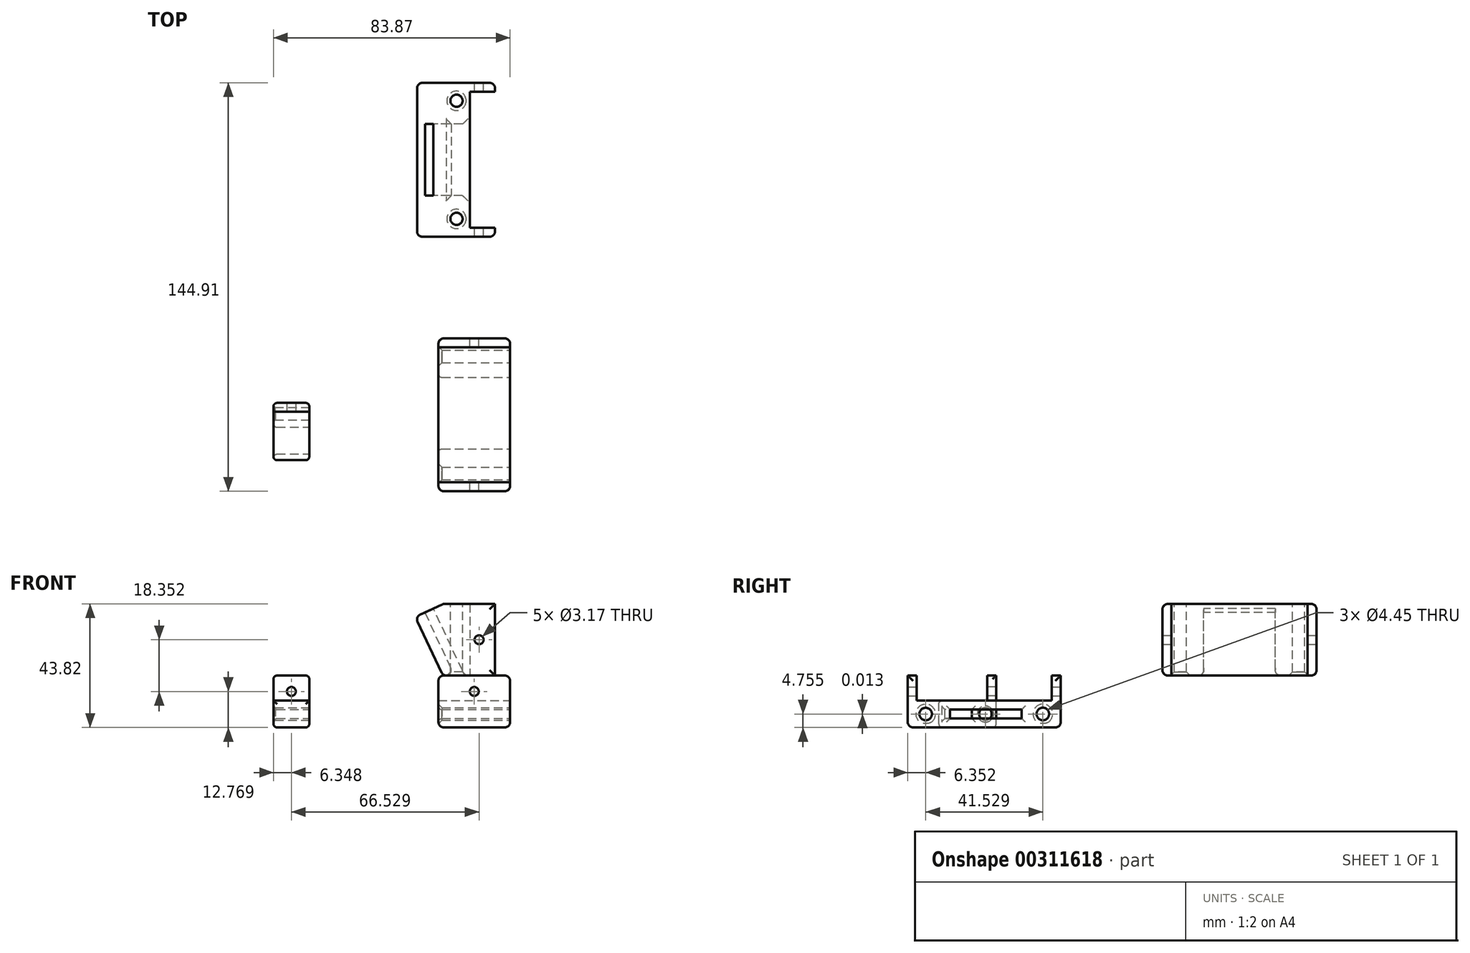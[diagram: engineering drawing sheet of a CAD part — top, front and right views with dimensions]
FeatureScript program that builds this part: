
annotation { "Feature Type Name" : "Feature", "Feature Type Description" : "" }
export const myFeature = defineFeature(function(context is Context, id is Id, definition is map)
    precondition{}
    {
        {
            var Q0;
            Q0=qCreatedBy(makeId("Top.planeOp"),FACE);
            var sketch = newSketch(context, id + "F0", { "sketchPlane" : qUnion([Q0])});
            skLineSegment(sketch, "E0.bottom", {"start": v(-15.61, -27.13) * mm, "end": v(9.79, -27.13) * mm});
            skLineSegment(sketch, "E0.top", {"start": v(-15.61, -30.3) * mm, "end": v(9.79, -30.3) * mm});
            skLineSegment(sketch, "E0.left", {"start": v(-15.61, -27.13) * mm, "end": v(-15.61, -30.3) * mm});
            skLineSegment(sketch, "E0.right", {"start": v(9.79, -27.13) * mm, "end": v(9.79, -30.3) * mm});
            skLineSegment(sketch, "E1.bottom", {"start": v(-15.61, 23.92) * mm, "end": v(9.79, 23.92) * mm});
            skLineSegment(sketch, "E1.top", {"start": v(-15.61, 20.75) * mm, "end": v(9.79, 20.75) * mm});
            skLineSegment(sketch, "E1.left", {"start": v(-15.61, 23.92) * mm, "end": v(-15.61, 20.75) * mm});
            skLineSegment(sketch, "E1.right", {"start": v(9.79, 23.92) * mm, "end": v(9.79, 20.75) * mm});
            skSolve(sketch);
        }
        {
            var Q0;
            Q0 = qSketchRegion(id + "F0", true);
            extrude(context, id + "F1", {"entities" : qUnion([Q0]), "depth" : 8.9 * mm});
        }
        {
            var Q0;
            Q0=makeQuery(id+"F1.opExtrude","CAP_FACE",FACE,{"disambiguationData":[OSD([sQuery(id+"F0.wireOp",EDGE,"E0.bottom"),sQuery(id+"F0.wireOp",EDGE,"E0.top"),sQuery(id+"F0.wireOp",EDGE,"E0.left"),sQuery(id+"F0.wireOp",EDGE,"E0.right")])],"isStart":false});
            var sketch = newSketch(context, id + "F2", { "sketchPlane" : qUnion([Q0])});
            skLineSegment(sketch, "E2.bottom", {"start": v(9.79, -30.3) * mm, "end": v(-15.61, -30.3) * mm});
            skLineSegment(sketch, "E2.top", {"start": v(9.79, 23.92) * mm, "end": v(-15.61, 23.92) * mm});
            skLineSegment(sketch, "E2.left", {"start": v(9.79, -30.3) * mm, "end": v(9.79, 23.92) * mm});
            skLineSegment(sketch, "E2.right", {"start": v(-15.61, -30.3) * mm, "end": v(-15.61, 23.92) * mm});
            skSolve(sketch);
        }
        {
            var Q0;
            Q0 = qSketchRegion(id + "F2", true);
            extrude(context, id + "F3", {"entities" : qUnion([Q0]), "depth" : 9.52 * mm});
        }
        {
            var Q0;
            Q0=makeQuery(id+"F1.opExtrude","SWEPT_BODY",BODY,{"disambiguationData":[OSD([sQuery(id+"F0.wireOp",EDGE,"E0.bottom"),sQuery(id+"F0.wireOp",EDGE,"E0.top"),sQuery(id+"F0.wireOp",EDGE,"E0.left"),sQuery(id+"F0.wireOp",EDGE,"E0.right")])]});
            var Q1;
            Q1=makeQuery(id+"F1.opExtrude","SWEPT_BODY",BODY,{"disambiguationData":[OSD([sQuery(id+"F0.wireOp",EDGE,"E1.bottom"),sQuery(id+"F0.wireOp",EDGE,"E1.top"),sQuery(id+"F0.wireOp",EDGE,"E1.left"),sQuery(id+"F0.wireOp",EDGE,"E1.right")])]});
            var Q2;
            Q2=makeQuery(id+"F3.opExtrude","SWEPT_BODY",BODY,{"disambiguationData":[OSD([sQuery(id+"F2.wireOp",EDGE,"E2.bottom"),sQuery(id+"F2.wireOp",EDGE,"E2.top"),sQuery(id+"F2.wireOp",EDGE,"E2.left"),sQuery(id+"F2.wireOp",EDGE,"E2.right")])]});
            booleanBodies(context, id + "F4", {"operationType" : BooleanOperationType.UNION, "tools" : qUnion([Q0, Q1, Q2])});
        }
        {
            var Q0;
            Q0=makeQuery(id+"F4.opBoolean","MERGE",FACE,{"derivedFrom":[makeQuery(id+"F1.opExtrude","SWEPT_FACE",FACE,{"disambiguationData":[OSD([sQuery(id+"F0.wireOp",EDGE,"E0.right")])]}),makeQuery(id+"F1.opExtrude","SWEPT_FACE",FACE,{"disambiguationData":[OSD([sQuery(id+"F0.wireOp",EDGE,"E1.right")])]}),makeQuery(id+"F3.opExtrude","SWEPT_FACE",FACE,{"disambiguationData":[OSD([sQuery(id+"F2.wireOp",EDGE,"E2.left")])]})]});
            var sketch = newSketch(context, id + "F5", { "sketchPlane" : qUnion([Q0])});
            skCircle(sketch, "E3", {"center": v(-23.96, 13.65) * mm, "radius": 2.22 * mm});
            skCircle(sketch, "E4", {"center": v(17.57, 13.67) * mm, "radius": 2.22 * mm});
            skLineSegment(sketch, "E5.bottom", {"start": v(-16.48, 15.24) * mm, "end": v(8.92, 15.24) * mm});
            skLineSegment(sketch, "E5.top", {"start": v(-16.48, 12.07) * mm, "end": v(8.92, 12.07) * mm});
            skLineSegment(sketch, "E5.left", {"start": v(-16.48, 15.24) * mm, "end": v(-16.48, 12.07) * mm});
            skLineSegment(sketch, "E5.right", {"start": v(8.92, 15.24) * mm, "end": v(8.92, 12.07) * mm});
            skSolve(sketch);
        }
        {
            var Q0;
            Q0 = qSketchRegion(id + "F5", true);
            extrude(context, id + "F6", {"entities" : qUnion([Q0]), "operationType" : NewBodyOperationType.REMOVE, "oppositeDirection" : true, "depth" : 50.8 * mm});
        }
        {
            var Q0;
            Q0=makeQuery(id+"F6.boolean.opBoolean","COPY",EDGE,{"derivedFrom":makeQuery(id+"F6.opExtrude","CAP_EDGE",EDGE,{"disambiguationData":[OSD([sQuery(id+"F5.wireOp",EDGE,"E5.bottom")])],"isStart":true})});
            var Q1;
            Q1=makeQuery(id+"F6.boolean.opBoolean","COPY",EDGE,{"derivedFrom":makeQuery(id+"F6.opExtrude","CAP_EDGE",EDGE,{"disambiguationData":[OSD([sQuery(id+"F5.wireOp",EDGE,"E5.left")])],"isStart":true})});
            var Q2;
            Q2=makeQuery(id+"F6.boolean.opBoolean","COPY",EDGE,{"derivedFrom":makeQuery(id+"F6.opExtrude","CAP_EDGE",EDGE,{"disambiguationData":[OSD([sQuery(id+"F5.wireOp",EDGE,"E5.top")])],"isStart":true})});
            var Q3;
            Q3=makeQuery(id+"F6.boolean.opBoolean","COPY",EDGE,{"derivedFrom":makeQuery(id+"F6.opExtrude","CAP_EDGE",EDGE,{"disambiguationData":[OSD([sQuery(id+"F5.wireOp",EDGE,"E5.right")])],"isStart":true})});
            var Q4;
            Q4=makeQuery(id+"F6.boolean.opBoolean","INTERSECT",EDGE,{"derivedFrom":[makeQuery(id+"F4.opBoolean","MERGE",FACE,{"derivedFrom":[makeQuery(id+"F1.opExtrude","SWEPT_FACE",FACE,{"disambiguationData":[OSD([sQuery(id+"F0.wireOp",EDGE,"E0.left")])]}),makeQuery(id+"F1.opExtrude","SWEPT_FACE",FACE,{"disambiguationData":[OSD([sQuery(id+"F0.wireOp",EDGE,"E1.left")])]}),makeQuery(id+"F3.opExtrude","SWEPT_FACE",FACE,{"disambiguationData":[OSD([sQuery(id+"F2.wireOp",EDGE,"E2.right")])]})]}),makeQuery(id+"F6.opExtrude","SWEPT_FACE",FACE,{"disambiguationData":[OSD([sQuery(id+"F5.wireOp",EDGE,"E5.right")])]})]});
            var Q5;
            Q5=makeQuery(id+"F6.boolean.opBoolean","INTERSECT",EDGE,{"derivedFrom":[makeQuery(id+"F4.opBoolean","MERGE",FACE,{"derivedFrom":[makeQuery(id+"F1.opExtrude","SWEPT_FACE",FACE,{"disambiguationData":[OSD([sQuery(id+"F0.wireOp",EDGE,"E0.left")])]}),makeQuery(id+"F1.opExtrude","SWEPT_FACE",FACE,{"disambiguationData":[OSD([sQuery(id+"F0.wireOp",EDGE,"E1.left")])]}),makeQuery(id+"F3.opExtrude","SWEPT_FACE",FACE,{"disambiguationData":[OSD([sQuery(id+"F2.wireOp",EDGE,"E2.right")])]})]}),makeQuery(id+"F6.opExtrude","SWEPT_FACE",FACE,{"disambiguationData":[OSD([sQuery(id+"F5.wireOp",EDGE,"E5.bottom")])]})]});
            var Q6;
            Q6=makeQuery(id+"F6.boolean.opBoolean","INTERSECT",EDGE,{"derivedFrom":[makeQuery(id+"F4.opBoolean","MERGE",FACE,{"derivedFrom":[makeQuery(id+"F1.opExtrude","SWEPT_FACE",FACE,{"disambiguationData":[OSD([sQuery(id+"F0.wireOp",EDGE,"E0.left")])]}),makeQuery(id+"F1.opExtrude","SWEPT_FACE",FACE,{"disambiguationData":[OSD([sQuery(id+"F0.wireOp",EDGE,"E1.left")])]}),makeQuery(id+"F3.opExtrude","SWEPT_FACE",FACE,{"disambiguationData":[OSD([sQuery(id+"F2.wireOp",EDGE,"E2.right")])]})]}),makeQuery(id+"F6.opExtrude","SWEPT_FACE",FACE,{"disambiguationData":[OSD([sQuery(id+"F5.wireOp",EDGE,"E5.top")])]})]});
            var Q7;
            Q7=makeQuery(id+"F6.boolean.opBoolean","INTERSECT",EDGE,{"derivedFrom":[makeQuery(id+"F4.opBoolean","MERGE",FACE,{"derivedFrom":[makeQuery(id+"F1.opExtrude","SWEPT_FACE",FACE,{"disambiguationData":[OSD([sQuery(id+"F0.wireOp",EDGE,"E0.left")])]}),makeQuery(id+"F1.opExtrude","SWEPT_FACE",FACE,{"disambiguationData":[OSD([sQuery(id+"F0.wireOp",EDGE,"E1.left")])]}),makeQuery(id+"F3.opExtrude","SWEPT_FACE",FACE,{"disambiguationData":[OSD([sQuery(id+"F2.wireOp",EDGE,"E2.right")])]})]}),makeQuery(id+"F6.opExtrude","SWEPT_FACE",FACE,{"disambiguationData":[OSD([sQuery(id+"F5.wireOp",EDGE,"E5.left")])]})]});
            fillet(context, id + "F7", {"entities" : qUnion([Q0, Q1, Q2, Q3, Q4, Q5, Q6, Q7]), "radius" : 1.27 * mm, "tangentPropagation" : true, "allowEdgeOverflow" : false});
        }
        {
            var Q0;
            Q0=makeQuery(id+"F6.boolean.opBoolean","INTERSECT",EDGE,{"derivedFrom":[makeQuery(id+"F4.opBoolean","MERGE",FACE,{"derivedFrom":[makeQuery(id+"F1.opExtrude","SWEPT_FACE",FACE,{"disambiguationData":[OSD([sQuery(id+"F0.wireOp",EDGE,"E0.left")])]}),makeQuery(id+"F1.opExtrude","SWEPT_FACE",FACE,{"disambiguationData":[OSD([sQuery(id+"F0.wireOp",EDGE,"E1.left")])]}),makeQuery(id+"F3.opExtrude","SWEPT_FACE",FACE,{"disambiguationData":[OSD([sQuery(id+"F2.wireOp",EDGE,"E2.right")])]})]}),makeQuery(id+"F6.opExtrude","SWEPT_FACE",FACE,{"disambiguationData":[OSD([sQuery(id+"F5.wireOp",EDGE,"E4")])]})]});
            var Q1;
            Q1=makeQuery(id+"F6.boolean.opBoolean","INTERSECT",EDGE,{"derivedFrom":[makeQuery(id+"F4.opBoolean","MERGE",FACE,{"derivedFrom":[makeQuery(id+"F1.opExtrude","SWEPT_FACE",FACE,{"disambiguationData":[OSD([sQuery(id+"F0.wireOp",EDGE,"E0.left")])]}),makeQuery(id+"F1.opExtrude","SWEPT_FACE",FACE,{"disambiguationData":[OSD([sQuery(id+"F0.wireOp",EDGE,"E1.left")])]}),makeQuery(id+"F3.opExtrude","SWEPT_FACE",FACE,{"disambiguationData":[OSD([sQuery(id+"F2.wireOp",EDGE,"E2.right")])]})]}),makeQuery(id+"F6.opExtrude","SWEPT_FACE",FACE,{"disambiguationData":[OSD([sQuery(id+"F5.wireOp",EDGE,"E3")])]})]});
            var Q2;
            Q2=makeQuery(id+"F6.boolean.opBoolean","COPY",EDGE,{"derivedFrom":makeQuery(id+"F6.opExtrude","CAP_EDGE",EDGE,{"disambiguationData":[OSD([sQuery(id+"F5.wireOp",EDGE,"E3")])],"isStart":true})});
            var Q3;
            Q3=makeQuery(id+"F6.boolean.opBoolean","COPY",EDGE,{"derivedFrom":makeQuery(id+"F6.opExtrude","CAP_EDGE",EDGE,{"disambiguationData":[OSD([sQuery(id+"F5.wireOp",EDGE,"E4")])],"isStart":true})});
            chamfer(context, id + "F8", {"entities" : qUnion([Q0, Q1, Q2, Q3]), "width" : 1.27 * mm, "tangentPropagation" : true});
        }
        {
            var Q0;
            Q0=makeQuery(id+"F3.opExtrude","CAP_EDGE",EDGE,{"disambiguationData":[OSD([sQuery(id+"F2.wireOp",EDGE,"E2.left")])],"isStart":false});
            var Q1;
            Q1=makeQuery(id+"F3.opExtrude","CAP_EDGE",EDGE,{"disambiguationData":[OSD([sQuery(id+"F2.wireOp",EDGE,"E2.bottom")])],"isStart":false});
            var Q2;
            Q2=makeQuery(id+"F3.opExtrude","CAP_EDGE",EDGE,{"disambiguationData":[OSD([sQuery(id+"F2.wireOp",EDGE,"E2.top")])],"isStart":false});
            var Q3;
            Q3=makeQuery(id+"F3.opExtrude","CAP_EDGE",EDGE,{"disambiguationData":[OSD([sQuery(id+"F2.wireOp",EDGE,"E2.right")])],"isStart":false});
            var Q4;
            Q4=makeQuery(id+"F1.opExtrude","CAP_EDGE",EDGE,{"disambiguationData":[OSD([sQuery(id+"F0.wireOp",EDGE,"E0.right")])],"isStart":true});
            var Q5;
            Q5=makeQuery(id+"F1.opExtrude","CAP_EDGE",EDGE,{"disambiguationData":[OSD([sQuery(id+"F0.wireOp",EDGE,"E1.right")])],"isStart":true});
            var Q6;
            Q6=makeQuery(id+"F4.opBoolean","MERGE",EDGE,{"derivedFrom":[makeQuery(id+"F1.opExtrude","SWEPT_EDGE",EDGE,{"disambiguationData":[OSD([sQuery(id+"F0.wireOp",EDGE,"E1.bottom"),sQuery(id+"F0.wireOp",EDGE,"E1.right")])]}),makeQuery(id+"F3.opExtrude","SWEPT_EDGE",EDGE,{"disambiguationData":[OSD([sQuery(id+"F2.wireOp",EDGE,"E2.top"),sQuery(id+"F2.wireOp",EDGE,"E2.left")])]})]});
            var Q7;
            Q7=makeQuery(id+"F4.opBoolean","MERGE",EDGE,{"derivedFrom":[makeQuery(id+"F1.opExtrude","SWEPT_EDGE",EDGE,{"disambiguationData":[OSD([sQuery(id+"F0.wireOp",EDGE,"E0.top"),sQuery(id+"F0.wireOp",EDGE,"E0.right")])]}),makeQuery(id+"F3.opExtrude","SWEPT_EDGE",EDGE,{"disambiguationData":[OSD([sQuery(id+"F2.wireOp",EDGE,"E2.bottom"),sQuery(id+"F2.wireOp",EDGE,"E2.left")])]})]});
            var Q8;
            Q8=makeQuery(id+"F4.opBoolean","MERGE",EDGE,{"derivedFrom":[makeQuery(id+"F1.opExtrude","SWEPT_EDGE",EDGE,{"disambiguationData":[OSD([sQuery(id+"F0.wireOp",EDGE,"E0.top"),sQuery(id+"F0.wireOp",EDGE,"E0.left")])]}),makeQuery(id+"F3.opExtrude","SWEPT_EDGE",EDGE,{"disambiguationData":[OSD([sQuery(id+"F2.wireOp",EDGE,"E2.bottom"),sQuery(id+"F2.wireOp",EDGE,"E2.right")])]})]});
            var Q9;
            Q9=makeQuery(id+"F1.opExtrude","CAP_EDGE",EDGE,{"disambiguationData":[OSD([sQuery(id+"F0.wireOp",EDGE,"E0.left")])],"isStart":true});
            var Q10;
            Q10=makeQuery(id+"F4.opBoolean","MERGE",EDGE,{"derivedFrom":[makeQuery(id+"F1.opExtrude","SWEPT_EDGE",EDGE,{"disambiguationData":[OSD([sQuery(id+"F0.wireOp",EDGE,"E1.bottom"),sQuery(id+"F0.wireOp",EDGE,"E1.left")])]}),makeQuery(id+"F3.opExtrude","SWEPT_EDGE",EDGE,{"disambiguationData":[OSD([sQuery(id+"F2.wireOp",EDGE,"E2.top"),sQuery(id+"F2.wireOp",EDGE,"E2.right")])]})]});
            var Q11;
            Q11=makeQuery(id+"F1.opExtrude","CAP_EDGE",EDGE,{"disambiguationData":[OSD([sQuery(id+"F0.wireOp",EDGE,"E1.left")])],"isStart":true});
            fillet(context, id + "F9", {"entities" : qUnion([Q0, Q1, Q2, Q3, Q4, Q5, Q6, Q7, Q8, Q9, Q10, Q11]), "radius" : 1.9 * mm, "tangentPropagation" : true, "allowEdgeOverflow" : false});
        }
        {
            var Q0;
            Q0=makeQuery(id+"F1.opExtrude","SWEPT_FACE",FACE,{"disambiguationData":[OSD([sQuery(id+"F0.wireOp",EDGE,"E1.top")])]});
            var sketch = newSketch(context, id + "F10", { "sketchPlane" : qUnion([Q0])});
            skCircle(sketch, "E6", {"center": v(-2.91, 5.65) * mm, "radius": 1.59 * mm});
            skSolve(sketch);
        }
        {
            var Q0;
            Q0 = qSketchRegion(id + "F10", true);
            extrude(context, id + "F11", {"entities" : qUnion([Q0]), "operationType" : NewBodyOperationType.REMOVE, "endBound" : BoundingType.SYMMETRIC, "oppositeDirection" : true, "depth" : 127 * mm});
        }
        {
            var Q0;
            Q0=qCreatedBy(makeId("Top.planeOp"),FACE);
            var sketch = newSketch(context, id + "F12", { "sketchPlane" : qUnion([Q0])});
            skLineSegment(sketch, "E7.bottom", {"start": v(-61.38, -53.2) * mm, "end": v(-74.08, -53.2) * mm});
            skLineSegment(sketch, "E7.top", {"start": v(-61.38, -50.03) * mm, "end": v(-74.08, -50.03) * mm});
            skLineSegment(sketch, "E7.left", {"start": v(-61.38, -53.2) * mm, "end": v(-61.38, -50.03) * mm});
            skLineSegment(sketch, "E7.right", {"start": v(-74.08, -53.2) * mm, "end": v(-74.08, -50.03) * mm});
            skSolve(sketch);
        }
        {
            var Q0;
            Q0=makeQuery(id+"F12.imprint","IMPRINT",FACE,{"disambiguationData":[TD([[makeQuery(id+"F12.imprint","IMPRINT",EDGE,{"derivedFrom":sQuery(id+"F12.wireOp",EDGE,"E7.bottom")}),-1.0]])]});
            extrude(context, id + "F13", {"entities" : qUnion([Q0]), "depth" : 8.9 * mm});
        }
        {
            var Q0;
            Q0=makeQuery(id+"F13.opExtrude","CAP_FACE",FACE,{"disambiguationData":[OSD([sQuery(id+"F12.wireOp",EDGE,"E7.bottom"),sQuery(id+"F12.wireOp",EDGE,"E7.top"),sQuery(id+"F12.wireOp",EDGE,"E7.left"),sQuery(id+"F12.wireOp",EDGE,"E7.right")])],"isStart":false});
            var sketch = newSketch(context, id + "F14", { "sketchPlane" : qUnion([Q0])});
            skLineSegment(sketch, "E8.bottom", {"start": v(-61.38, -50.03) * mm, "end": v(-74.08, -50.03) * mm});
            skLineSegment(sketch, "E8.top", {"start": v(-61.38, -32.88) * mm, "end": v(-74.08, -32.88) * mm});
            skLineSegment(sketch, "E8.left", {"start": v(-61.38, -50.03) * mm, "end": v(-61.38, -32.88) * mm});
            skLineSegment(sketch, "E8.right", {"start": v(-74.08, -50.03) * mm, "end": v(-74.08, -32.88) * mm});
            skLineSegment(sketch, "E9.bottom", {"start": v(-74.08, -50.03) * mm, "end": v(-61.38, -50.03) * mm});
            skLineSegment(sketch, "E9.top", {"start": v(-74.08, -53.2) * mm, "end": v(-61.38, -53.2) * mm});
            skLineSegment(sketch, "E9.left", {"start": v(-74.08, -50.03) * mm, "end": v(-74.08, -53.2) * mm});
            skLineSegment(sketch, "E9.right", {"start": v(-61.38, -50.03) * mm, "end": v(-61.38, -53.2) * mm});
            skSolve(sketch);
        }
        {
            var Q0;
            Q0 = qSketchRegion(id + "F14", true);
            extrude(context, id + "F15", {"entities" : qUnion([Q0]), "operationType" : NewBodyOperationType.ADD, "depth" : 9.52 * mm});
        }
        {
            var Q0;
            Q0=makeQuery(id+"F15.boolean.opBoolean","MERGE",FACE,{"derivedFrom":[makeQuery(id+"F13.opExtrude","SWEPT_FACE",FACE,{"disambiguationData":[OSD([sQuery(id+"F12.wireOp",EDGE,"E7.left")])]}),makeQuery(id+"F15.opExtrude","SWEPT_FACE",FACE,{"disambiguationData":[OSD([sQuery(id+"F14.wireOp",EDGE,"E8.left"),sQuery(id+"F14.wireOp",EDGE,"E9.right")])]})]});
            var sketch = newSketch(context, id + "F16", { "sketchPlane" : qUnion([Q0])});
            skCircle(sketch, "E10", {"center": v(-49.4, 13.65) * mm, "radius": 2.22 * mm});
            skLineSegment(sketch, "E11.bottom", {"start": v(-44.57, 15.23) * mm, "end": v(-35.04, 15.23) * mm});
            skLineSegment(sketch, "E11.top", {"start": v(-44.57, 12.06) * mm, "end": v(-35.04, 12.06) * mm});
            skLineSegment(sketch, "E11.left", {"start": v(-44.57, 15.23) * mm, "end": v(-44.57, 12.06) * mm});
            skLineSegment(sketch, "E11.right", {"start": v(-35.04, 15.23) * mm, "end": v(-35.04, 12.06) * mm});
            skSolve(sketch);
        }
        {
            var Q0;
            Q0 = qSketchRegion(id + "F16", true);
            extrude(context, id + "F17", {"entities" : qUnion([Q0]), "operationType" : NewBodyOperationType.REMOVE, "oppositeDirection" : true, "depth" : 25.4 * mm});
        }
        {
            var Q0;
            Q0=makeQuery(id+"F17.boolean.opBoolean","COPY",EDGE,{"derivedFrom":makeQuery(id+"F17.opExtrude","CAP_EDGE",EDGE,{"disambiguationData":[OSD([sQuery(id+"F16.wireOp",EDGE,"E11.bottom")])],"isStart":true})});
            var Q1;
            Q1=makeQuery(id+"F17.boolean.opBoolean","COPY",EDGE,{"derivedFrom":makeQuery(id+"F17.opExtrude","CAP_EDGE",EDGE,{"disambiguationData":[OSD([sQuery(id+"F16.wireOp",EDGE,"E11.left")])],"isStart":true})});
            var Q2;
            Q2=makeQuery(id+"F17.boolean.opBoolean","COPY",EDGE,{"derivedFrom":makeQuery(id+"F17.opExtrude","CAP_EDGE",EDGE,{"disambiguationData":[OSD([sQuery(id+"F16.wireOp",EDGE,"E11.top")])],"isStart":true})});
            var Q3;
            Q3=makeQuery(id+"F17.boolean.opBoolean","COPY",EDGE,{"derivedFrom":makeQuery(id+"F17.opExtrude","CAP_EDGE",EDGE,{"disambiguationData":[OSD([sQuery(id+"F16.wireOp",EDGE,"E11.right")])],"isStart":true})});
            var Q4;
            Q4=makeQuery(id+"F17.boolean.opBoolean","INTERSECT",EDGE,{"derivedFrom":[makeQuery(id+"F15.boolean.opBoolean","MERGE",FACE,{"derivedFrom":[makeQuery(id+"F13.opExtrude","SWEPT_FACE",FACE,{"disambiguationData":[OSD([sQuery(id+"F12.wireOp",EDGE,"E7.right")])]}),makeQuery(id+"F15.opExtrude","SWEPT_FACE",FACE,{"disambiguationData":[OSD([sQuery(id+"F14.wireOp",EDGE,"E8.right"),sQuery(id+"F14.wireOp",EDGE,"E9.left")])]})]}),makeQuery(id+"F17.opExtrude","SWEPT_FACE",FACE,{"disambiguationData":[OSD([sQuery(id+"F16.wireOp",EDGE,"E11.bottom")])]})]});
            var Q5;
            Q5=makeQuery(id+"F17.boolean.opBoolean","INTERSECT",EDGE,{"derivedFrom":[makeQuery(id+"F15.boolean.opBoolean","MERGE",FACE,{"derivedFrom":[makeQuery(id+"F13.opExtrude","SWEPT_FACE",FACE,{"disambiguationData":[OSD([sQuery(id+"F12.wireOp",EDGE,"E7.right")])]}),makeQuery(id+"F15.opExtrude","SWEPT_FACE",FACE,{"disambiguationData":[OSD([sQuery(id+"F14.wireOp",EDGE,"E8.right"),sQuery(id+"F14.wireOp",EDGE,"E9.left")])]})]}),makeQuery(id+"F17.opExtrude","SWEPT_FACE",FACE,{"disambiguationData":[OSD([sQuery(id+"F16.wireOp",EDGE,"E11.right")])]})]});
            var Q6;
            Q6=makeQuery(id+"F17.boolean.opBoolean","INTERSECT",EDGE,{"derivedFrom":[makeQuery(id+"F15.boolean.opBoolean","MERGE",FACE,{"derivedFrom":[makeQuery(id+"F13.opExtrude","SWEPT_FACE",FACE,{"disambiguationData":[OSD([sQuery(id+"F12.wireOp",EDGE,"E7.right")])]}),makeQuery(id+"F15.opExtrude","SWEPT_FACE",FACE,{"disambiguationData":[OSD([sQuery(id+"F14.wireOp",EDGE,"E8.right"),sQuery(id+"F14.wireOp",EDGE,"E9.left")])]})]}),makeQuery(id+"F17.opExtrude","SWEPT_FACE",FACE,{"disambiguationData":[OSD([sQuery(id+"F16.wireOp",EDGE,"E11.top")])]})]});
            var Q7;
            Q7=makeQuery(id+"F17.boolean.opBoolean","INTERSECT",EDGE,{"derivedFrom":[makeQuery(id+"F15.boolean.opBoolean","MERGE",FACE,{"derivedFrom":[makeQuery(id+"F13.opExtrude","SWEPT_FACE",FACE,{"disambiguationData":[OSD([sQuery(id+"F12.wireOp",EDGE,"E7.right")])]}),makeQuery(id+"F15.opExtrude","SWEPT_FACE",FACE,{"disambiguationData":[OSD([sQuery(id+"F14.wireOp",EDGE,"E8.right"),sQuery(id+"F14.wireOp",EDGE,"E9.left")])]})]}),makeQuery(id+"F17.opExtrude","SWEPT_FACE",FACE,{"disambiguationData":[OSD([sQuery(id+"F16.wireOp",EDGE,"E11.left")])]})]});
            fillet(context, id + "F18", {"entities" : qUnion([Q0, Q1, Q2, Q3, Q4, Q5, Q6, Q7]), "radius" : 1.27 * mm, "tangentPropagation" : true, "allowEdgeOverflow" : false});
        }
        {
            var Q0;
            Q0=makeQuery(id+"F17.boolean.opBoolean","INTERSECT",EDGE,{"derivedFrom":[makeQuery(id+"F15.boolean.opBoolean","MERGE",FACE,{"derivedFrom":[makeQuery(id+"F13.opExtrude","SWEPT_FACE",FACE,{"disambiguationData":[OSD([sQuery(id+"F12.wireOp",EDGE,"E7.right")])]}),makeQuery(id+"F15.opExtrude","SWEPT_FACE",FACE,{"disambiguationData":[OSD([sQuery(id+"F14.wireOp",EDGE,"E8.right"),sQuery(id+"F14.wireOp",EDGE,"E9.left")])]})]}),makeQuery(id+"F17.opExtrude","SWEPT_FACE",FACE,{"disambiguationData":[OSD([sQuery(id+"F16.wireOp",EDGE,"E10")])]})]});
            var Q1;
            Q1=makeQuery(id+"F17.boolean.opBoolean","COPY",EDGE,{"derivedFrom":makeQuery(id+"F17.opExtrude","CAP_EDGE",EDGE,{"disambiguationData":[OSD([sQuery(id+"F16.wireOp",EDGE,"E10")])],"isStart":true})});
            chamfer(context, id + "F19", {"entities" : qUnion([Q0, Q1]), "width" : 0.64 * mm, "tangentPropagation" : true});
        }
        {
            var Q0;
            Q0=makeQuery(id+"F15.opExtrude","CAP_FACE",FACE,{"disambiguationData":[OSD([sQuery(id+"F14.wireOp",EDGE,"E8.top"),sQuery(id+"F14.wireOp",EDGE,"E8.left"),sQuery(id+"F14.wireOp",EDGE,"E8.right"),sQuery(id+"F14.wireOp",EDGE,"E9.top"),sQuery(id+"F14.wireOp",EDGE,"E9.left"),sQuery(id+"F14.wireOp",EDGE,"E9.right")])],"isStart":false});
            var Q1;
            Q1=makeQuery(id+"F15.boolean.opBoolean","MERGE",EDGE,{"derivedFrom":[makeQuery(id+"F13.opExtrude","SWEPT_EDGE",EDGE,{"disambiguationData":[OSD([sQuery(id+"F12.wireOp",EDGE,"E7.bottom"),sQuery(id+"F12.wireOp",EDGE,"E7.left")])]}),makeQuery(id+"F15.opExtrude","SWEPT_EDGE",EDGE,{"disambiguationData":[OSD([sQuery(id+"F14.wireOp",EDGE,"E9.top"),sQuery(id+"F14.wireOp",EDGE,"E9.right")])]})]});
            var Q2;
            Q2=makeQuery(id+"F15.boolean.opBoolean","MERGE",EDGE,{"derivedFrom":[makeQuery(id+"F13.opExtrude","SWEPT_EDGE",EDGE,{"disambiguationData":[OSD([sQuery(id+"F12.wireOp",EDGE,"E7.bottom"),sQuery(id+"F12.wireOp",EDGE,"E7.right")])]}),makeQuery(id+"F15.opExtrude","SWEPT_EDGE",EDGE,{"disambiguationData":[OSD([sQuery(id+"F14.wireOp",EDGE,"E9.top"),sQuery(id+"F14.wireOp",EDGE,"E9.left")])]})]});
            var Q3;
            Q3=makeQuery(id+"F13.opExtrude","CAP_EDGE",EDGE,{"disambiguationData":[OSD([sQuery(id+"F12.wireOp",EDGE,"E7.left")])],"isStart":true});
            var Q4;
            Q4=makeQuery(id+"F15.opExtrude","SWEPT_EDGE",EDGE,{"disambiguationData":[OSD([sQuery(id+"F14.wireOp",EDGE,"E8.top"),sQuery(id+"F14.wireOp",EDGE,"E8.left")])]});
            var Q5;
            Q5=makeQuery(id+"F15.opExtrude","CAP_EDGE",EDGE,{"disambiguationData":[OSD([sQuery(id+"F14.wireOp",EDGE,"E8.top")])],"isStart":true});
            var Q6;
            Q6=makeQuery(id+"F15.opExtrude","SWEPT_EDGE",EDGE,{"disambiguationData":[OSD([sQuery(id+"F14.wireOp",EDGE,"E8.top"),sQuery(id+"F14.wireOp",EDGE,"E8.right")])]});
            var Q7;
            Q7=makeQuery(id+"F13.opExtrude","CAP_EDGE",EDGE,{"disambiguationData":[OSD([sQuery(id+"F12.wireOp",EDGE,"E7.right")])],"isStart":true});
            fillet(context, id + "F20", {"entities" : qUnion([Q0, Q1, Q2, Q3, Q4, Q5, Q6, Q7]), "radius" : 1.27 * mm, "tangentPropagation" : true, "allowEdgeOverflow" : false});
        }
        {
            var Q0;
            Q0=makeQuery(id+"F13.opExtrude","SWEPT_FACE",FACE,{"disambiguationData":[OSD([sQuery(id+"F12.wireOp",EDGE,"E7.top")])]});
            var sketch = newSketch(context, id + "F21", { "sketchPlane" : qUnion([Q0])});
            skCircle(sketch, "E12", {"center": v(67.73, 5.65) * mm, "radius": 1.59 * mm});
            skSolve(sketch);
        }
        {
            var Q0;
            Q0=makeQuery(id+"F21.imprint","IMPRINT",FACE,{"disambiguationData":[TD([[makeQuery(id+"F21.imprint","IMPRINT",EDGE,{"derivedFrom":sQuery(id+"F21.wireOp",EDGE,"E12")}),1.0]])]});
            extrude(context, id + "F22", {"entities" : qUnion([Q0]), "operationType" : NewBodyOperationType.REMOVE, "oppositeDirection" : true, "depth" : 25.4 * mm});
        }
        {
            var Q0;
            Q0=makeQuery(id+"F1.opExtrude","SWEPT_BODY",BODY,{"disambiguationData":[OSD([sQuery(id+"F0.wireOp",EDGE,"E0.bottom"),sQuery(id+"F0.wireOp",EDGE,"E0.top"),sQuery(id+"F0.wireOp",EDGE,"E0.left"),sQuery(id+"F0.wireOp",EDGE,"E0.right")])]});
            var Q1;
            Q1=makeQuery(id+"F1.opExtrude","CAP_EDGE",EDGE,{"disambiguationData":[OSD([sQuery(id+"F0.wireOp",EDGE,"E0.top")])],"isStart":true});
            var Q2;
            Q2=makeQuery(id+"F1.opExtrude","CAP_EDGE",EDGE,{"disambiguationData":[OSD([sQuery(id+"F0.wireOp",EDGE,"E0.top")])],"isStart":true});
            transform(context, id + "F23", {"entities" : qUnion([Q0]), "transformType" : TransformType.ROTATION, "transformAxis" : qUnion([Q2]), "angle" : 180 * degree, "makeCopy" : false});
        }
        {
            var Q0;
            Q0=makeQuery(id+"F13.opExtrude","SWEPT_BODY",BODY,{"disambiguationData":[OSD([sQuery(id+"F12.wireOp",EDGE,"E7.bottom"),sQuery(id+"F12.wireOp",EDGE,"E7.top"),sQuery(id+"F12.wireOp",EDGE,"E7.left"),sQuery(id+"F12.wireOp",EDGE,"E7.right")])]});
            var Q1;
            Q1=makeQuery(id+"F13.opExtrude","CAP_EDGE",EDGE,{"disambiguationData":[OSD([sQuery(id+"F12.wireOp",EDGE,"E7.bottom")])],"isStart":true});
            transform(context, id + "F24", {"entities" : qUnion([Q0]), "transformType" : TransformType.ROTATION, "transformAxis" : qUnion([Q1]), "angle" : 180 * degree, "makeCopy" : false});
        }
        {
            var Q0;
            Q0=qCreatedBy(makeId("Top.planeOp"),FACE);
            var sketch = newSketch(context, id + "F25", { "sketchPlane" : qUnion([Q0])});
            skLineSegment(sketch, "E13.bottom", {"start": v(-13.97, 60.37) * mm, "end": v(-4.44, 60.37) * mm});
            skLineSegment(sketch, "E13.top", {"start": v(-13.97, 5.76) * mm, "end": v(-4.44, 5.76) * mm});
            skLineSegment(sketch, "E13.left", {"start": v(-13.97, 60.37) * mm, "end": v(-13.97, 5.76) * mm});
            skLineSegment(sketch, "E13.right", {"start": v(-4.44, 60.37) * mm, "end": v(-4.44, 5.76) * mm});
            skLineSegment(sketch, "E14.bottom", {"start": v(-4.44, 5.76) * mm, "end": v(4.45, 5.76) * mm});
            skLineSegment(sketch, "E14.top", {"start": v(-4.44, 8.93) * mm, "end": v(4.45, 8.93) * mm});
            skLineSegment(sketch, "E14.left", {"start": v(-4.44, 5.76) * mm, "end": v(-4.44, 8.93) * mm});
            skLineSegment(sketch, "E14.right", {"start": v(4.45, 5.76) * mm, "end": v(4.45, 8.93) * mm});
            skLineSegment(sketch, "E15.bottom", {"start": v(-4.44, 60.37) * mm, "end": v(4.45, 60.37) * mm});
            skLineSegment(sketch, "E15.top", {"start": v(-4.44, 57.2) * mm, "end": v(4.45, 57.2) * mm});
            skLineSegment(sketch, "E15.left", {"start": v(-4.44, 60.37) * mm, "end": v(-4.44, 57.2) * mm});
            skLineSegment(sketch, "E15.right", {"start": v(4.45, 60.37) * mm, "end": v(4.45, 57.2) * mm});
            skSolve(sketch);
        }
        {
            var Q0;
            Q0 = qSketchRegion(id + "F25", true);
            extrude(context, id + "F26", {"entities" : qUnion([Q0]), "depth" : 25.4 * mm});
        }
        {
            var Q0;
            Q0=makeQuery(id+"F26.opExtrude","SWEPT_FACE",FACE,{"disambiguationData":[OSD([sQuery(id+"F25.wireOp",EDGE,"E13.top"),sQuery(id+"F25.wireOp",EDGE,"E14.bottom")])]});
            var sketch = newSketch(context, id + "F27", { "sketchPlane" : qUnion([Q0])});
            skLineSegment(sketch, "E16", {"start": v(-13.97, 0) * mm, "end": v(-23.83, 20.8) * mm});
            skLineSegment(sketch, "E17", {"start": v(-13.97, 25.4) * mm, "end": v(-23.83, 20.8) * mm});
            skSolve(sketch);
        }
        {
            var Q0;
            Q0=makeQuery(id+"F26.opExtrude","SWEPT_FACE",FACE,{"disambiguationData":[OSD([sQuery(id+"F25.wireOp",EDGE,"E13.bottom"),sQuery(id+"F25.wireOp",EDGE,"E15.bottom")])]});
            var sketch = newSketch(context, id + "F28", { "sketchPlane" : qUnion([Q0])});
            skLineSegment(sketch, "E18", {"start": v(13.97, 0) * mm, "end": v(23.7, 20.86) * mm});
            skLineSegment(sketch, "E19", {"start": v(13.97, 25.4) * mm, "end": v(23.7, 20.86) * mm});
            skSolve(sketch);
        }
        {
            var Q0;
            Q0=makeQuery(id+"F27.imprint","IMPRINT",FACE,{"disambiguationData":[TD([[makeQuery(id+"F27.imprint","IMPRINT",EDGE,{"derivedFrom":sQuery(id+"F27.wireOp",EDGE,"E16")}),-1.0]])]});
            extrude(context, id + "F29", {"entities" : qUnion([Q0]), "oppositeDirection" : true, "depth" : 54.6 * mm});
        }
        {
            var Q0;
            Q0=makeQuery(id+"F26.opExtrude","SWEPT_BODY",BODY,{"disambiguationData":[OSD([sQuery(id+"F25.wireOp",EDGE,"E13.bottom"),sQuery(id+"F25.wireOp",EDGE,"E13.top"),sQuery(id+"F25.wireOp",EDGE,"E13.left"),sQuery(id+"F25.wireOp",EDGE,"E13.right"),sQuery(id+"F25.wireOp",EDGE,"E14.bottom"),sQuery(id+"F25.wireOp",EDGE,"E14.top"),sQuery(id+"F25.wireOp",EDGE,"E14.right"),sQuery(id+"F25.wireOp",EDGE,"E15.bottom"),sQuery(id+"F25.wireOp",EDGE,"E15.top"),sQuery(id+"F25.wireOp",EDGE,"E15.right")])]});
            var Q1;
            Q1=makeQuery(id+"F29.opExtrude","SWEPT_BODY",BODY,{"disambiguationData":[OSD([sQuery(id+"F25.wireOp",EDGE,"E13.top"),sQuery(id+"F25.wireOp",EDGE,"E13.left"),sQuery(id+"F27.wireOp",EDGE,"E16"),sQuery(id+"F27.wireOp",EDGE,"E17")])]});
            booleanBodies(context, id + "F30", {"operationType" : BooleanOperationType.UNION, "tools" : qUnion([Q0, Q1])});
        }
        {
            var Q0;
            Q0=makeQuery(id+"F29.opExtrude","SWEPT_FACE",FACE,{"disambiguationData":[OSD([sQuery(id+"F27.wireOp",EDGE,"E17")])]});
            var sketch = newSketch(context, id + "F31", { "sketchPlane" : qUnion([Q0])});
            skLineSegment(sketch, "E20.bottom", {"start": v(-5.72, 45.76) * mm, "end": v(-9.02, 45.76) * mm});
            skLineSegment(sketch, "E20.top", {"start": v(-5.72, 20.36) * mm, "end": v(-9.02, 20.36) * mm});
            skLineSegment(sketch, "E20.left", {"start": v(-5.72, 45.76) * mm, "end": v(-5.72, 20.36) * mm});
            skLineSegment(sketch, "E20.right", {"start": v(-9.02, 45.76) * mm, "end": v(-9.02, 20.36) * mm});
            skSolve(sketch);
        }
        {
            var Q0;
            Q0=makeQuery(id+"F31.imprint","IMPRINT",FACE,{"disambiguationData":[TD([[makeQuery(id+"F31.imprint","IMPRINT",EDGE,{"derivedFrom":sQuery(id+"F31.wireOp",EDGE,"E20.bottom")}),1.0]])]});
            extrude(context, id + "F32", {"entities" : qUnion([Q0]), "operationType" : NewBodyOperationType.REMOVE, "oppositeDirection" : true, "depth" : 50.8 * mm});
        }
        {
            var Q0;
            Q0=makeQuery(id+"F32.boolean.opBoolean","COPY",EDGE,{"derivedFrom":makeQuery(id+"F32.opExtrude","CAP_EDGE",EDGE,{"disambiguationData":[OSD([sQuery(id+"F31.wireOp",EDGE,"E20.left")])],"isStart":true})});
            var Q1;
            Q1=makeQuery(id+"F32.boolean.opBoolean","COPY",EDGE,{"derivedFrom":makeQuery(id+"F32.opExtrude","CAP_EDGE",EDGE,{"disambiguationData":[OSD([sQuery(id+"F31.wireOp",EDGE,"E20.right")])],"isStart":true})});
            var Q2;
            Q2=makeQuery(id+"F32.boolean.opBoolean","COPY",EDGE,{"derivedFrom":makeQuery(id+"F32.opExtrude","CAP_EDGE",EDGE,{"disambiguationData":[OSD([sQuery(id+"F31.wireOp",EDGE,"E20.top")])],"isStart":true})});
            var Q3;
            Q3=makeQuery(id+"F32.boolean.opBoolean","COPY",EDGE,{"derivedFrom":makeQuery(id+"F32.opExtrude","CAP_EDGE",EDGE,{"disambiguationData":[OSD([sQuery(id+"F31.wireOp",EDGE,"E20.bottom")])],"isStart":true})});
            var Q4;
            Q4=makeQuery(id+"F32.boolean.opBoolean","INTERSECT",EDGE,{"derivedFrom":[makeQuery(id+"F26.opExtrude","CAP_FACE",FACE,{"disambiguationData":[OSD([sQuery(id+"F25.wireOp",EDGE,"E13.bottom"),sQuery(id+"F25.wireOp",EDGE,"E13.top"),sQuery(id+"F25.wireOp",EDGE,"E13.left"),sQuery(id+"F25.wireOp",EDGE,"E13.right"),sQuery(id+"F25.wireOp",EDGE,"E14.bottom"),sQuery(id+"F25.wireOp",EDGE,"E14.top"),sQuery(id+"F25.wireOp",EDGE,"E14.right"),sQuery(id+"F25.wireOp",EDGE,"E15.bottom"),sQuery(id+"F25.wireOp",EDGE,"E15.top"),sQuery(id+"F25.wireOp",EDGE,"E15.right")])],"isStart":true}),makeQuery(id+"F32.opExtrude","SWEPT_FACE",FACE,{"disambiguationData":[OSD([sQuery(id+"F31.wireOp",EDGE,"E20.right")])]})]});
            var Q5;
            Q5=makeQuery(id+"F32.boolean.opBoolean","INTERSECT",EDGE,{"derivedFrom":[makeQuery(id+"F26.opExtrude","CAP_FACE",FACE,{"disambiguationData":[OSD([sQuery(id+"F25.wireOp",EDGE,"E13.bottom"),sQuery(id+"F25.wireOp",EDGE,"E13.top"),sQuery(id+"F25.wireOp",EDGE,"E13.left"),sQuery(id+"F25.wireOp",EDGE,"E13.right"),sQuery(id+"F25.wireOp",EDGE,"E14.bottom"),sQuery(id+"F25.wireOp",EDGE,"E14.top"),sQuery(id+"F25.wireOp",EDGE,"E14.right"),sQuery(id+"F25.wireOp",EDGE,"E15.bottom"),sQuery(id+"F25.wireOp",EDGE,"E15.top"),sQuery(id+"F25.wireOp",EDGE,"E15.right")])],"isStart":true}),makeQuery(id+"F32.opExtrude","SWEPT_FACE",FACE,{"disambiguationData":[OSD([sQuery(id+"F31.wireOp",EDGE,"E20.top")])]})]});
            var Q6;
            Q6=makeQuery(id+"F32.boolean.opBoolean","INTERSECT",EDGE,{"derivedFrom":[makeQuery(id+"F26.opExtrude","CAP_FACE",FACE,{"disambiguationData":[OSD([sQuery(id+"F25.wireOp",EDGE,"E13.bottom"),sQuery(id+"F25.wireOp",EDGE,"E13.top"),sQuery(id+"F25.wireOp",EDGE,"E13.left"),sQuery(id+"F25.wireOp",EDGE,"E13.right"),sQuery(id+"F25.wireOp",EDGE,"E14.bottom"),sQuery(id+"F25.wireOp",EDGE,"E14.top"),sQuery(id+"F25.wireOp",EDGE,"E14.right"),sQuery(id+"F25.wireOp",EDGE,"E15.bottom"),sQuery(id+"F25.wireOp",EDGE,"E15.top"),sQuery(id+"F25.wireOp",EDGE,"E15.right")])],"isStart":true}),makeQuery(id+"F32.opExtrude","SWEPT_FACE",FACE,{"disambiguationData":[OSD([sQuery(id+"F31.wireOp",EDGE,"E20.bottom")])]})]});
            var Q7;
            Q7=makeQuery(id+"F32.boolean.opBoolean","INTERSECT",EDGE,{"derivedFrom":[makeQuery(id+"F26.opExtrude","CAP_FACE",FACE,{"disambiguationData":[OSD([sQuery(id+"F25.wireOp",EDGE,"E13.bottom"),sQuery(id+"F25.wireOp",EDGE,"E13.top"),sQuery(id+"F25.wireOp",EDGE,"E13.left"),sQuery(id+"F25.wireOp",EDGE,"E13.right"),sQuery(id+"F25.wireOp",EDGE,"E14.bottom"),sQuery(id+"F25.wireOp",EDGE,"E14.top"),sQuery(id+"F25.wireOp",EDGE,"E14.right"),sQuery(id+"F25.wireOp",EDGE,"E15.bottom"),sQuery(id+"F25.wireOp",EDGE,"E15.top"),sQuery(id+"F25.wireOp",EDGE,"E15.right")])],"isStart":true}),makeQuery(id+"F32.opExtrude","SWEPT_FACE",FACE,{"disambiguationData":[OSD([sQuery(id+"F31.wireOp",EDGE,"E20.left")])]})]});
            fillet(context, id + "F33", {"entities" : qUnion([Q0, Q1, Q2, Q3, Q4, Q5, Q6, Q7]), "radius" : 1.9 * mm, "tangentPropagation" : true, "allowEdgeOverflow" : false});
        }
        {
            var Q0;
            Q0=makeQuery(id+"F26.opExtrude","CAP_FACE",FACE,{"disambiguationData":[OSD([sQuery(id+"F25.wireOp",EDGE,"E13.bottom"),sQuery(id+"F25.wireOp",EDGE,"E13.top"),sQuery(id+"F25.wireOp",EDGE,"E13.left"),sQuery(id+"F25.wireOp",EDGE,"E13.right"),sQuery(id+"F25.wireOp",EDGE,"E14.bottom"),sQuery(id+"F25.wireOp",EDGE,"E14.top"),sQuery(id+"F25.wireOp",EDGE,"E14.right"),sQuery(id+"F25.wireOp",EDGE,"E15.bottom"),sQuery(id+"F25.wireOp",EDGE,"E15.top"),sQuery(id+"F25.wireOp",EDGE,"E15.right")])],"isStart":false});
            var sketch = newSketch(context, id + "F34", { "sketchPlane" : qUnion([Q0])});
            skCircle(sketch, "E21", {"center": v(-9.2, 12.1) * mm, "radius": 2.16 * mm});
            skCircle(sketch, "E22", {"center": v(-9.2, 54.02) * mm, "radius": 2.16 * mm});
            skSolve(sketch);
        }
        {
            var Q0;
            Q0 = qSketchRegion(id + "F34", true);
            extrude(context, id + "F35", {"entities" : qUnion([Q0]), "operationType" : NewBodyOperationType.REMOVE, "oppositeDirection" : true, "depth" : 50.8 * mm});
        }
        {
            var Q0;
            Q0=makeQuery(id+"F35.boolean.opBoolean","COPY",EDGE,{"derivedFrom":makeQuery(id+"F35.opExtrude","CAP_EDGE",EDGE,{"disambiguationData":[OSD([sQuery(id+"F34.wireOp",EDGE,"E21")])],"isStart":true})});
            var Q1;
            Q1=makeQuery(id+"F35.boolean.opBoolean","COPY",EDGE,{"derivedFrom":makeQuery(id+"F35.opExtrude","CAP_EDGE",EDGE,{"disambiguationData":[OSD([sQuery(id+"F34.wireOp",EDGE,"E22")])],"isStart":true})});
            var Q2;
            Q2=makeQuery(id+"F35.boolean.opBoolean","INTERSECT",EDGE,{"derivedFrom":[makeQuery(id+"F26.opExtrude","CAP_FACE",FACE,{"disambiguationData":[OSD([sQuery(id+"F25.wireOp",EDGE,"E13.bottom"),sQuery(id+"F25.wireOp",EDGE,"E13.top"),sQuery(id+"F25.wireOp",EDGE,"E13.left"),sQuery(id+"F25.wireOp",EDGE,"E13.right"),sQuery(id+"F25.wireOp",EDGE,"E14.bottom"),sQuery(id+"F25.wireOp",EDGE,"E14.top"),sQuery(id+"F25.wireOp",EDGE,"E14.right"),sQuery(id+"F25.wireOp",EDGE,"E15.bottom"),sQuery(id+"F25.wireOp",EDGE,"E15.top"),sQuery(id+"F25.wireOp",EDGE,"E15.right")])],"isStart":true}),makeQuery(id+"F35.opExtrude","SWEPT_FACE",FACE,{"disambiguationData":[OSD([sQuery(id+"F34.wireOp",EDGE,"E21")])]})]});
            var Q3;
            Q3=makeQuery(id+"F35.boolean.opBoolean","INTERSECT",EDGE,{"derivedFrom":[makeQuery(id+"F26.opExtrude","CAP_FACE",FACE,{"disambiguationData":[OSD([sQuery(id+"F25.wireOp",EDGE,"E13.bottom"),sQuery(id+"F25.wireOp",EDGE,"E13.top"),sQuery(id+"F25.wireOp",EDGE,"E13.left"),sQuery(id+"F25.wireOp",EDGE,"E13.right"),sQuery(id+"F25.wireOp",EDGE,"E14.bottom"),sQuery(id+"F25.wireOp",EDGE,"E14.top"),sQuery(id+"F25.wireOp",EDGE,"E14.right"),sQuery(id+"F25.wireOp",EDGE,"E15.bottom"),sQuery(id+"F25.wireOp",EDGE,"E15.top"),sQuery(id+"F25.wireOp",EDGE,"E15.right")])],"isStart":true}),makeQuery(id+"F35.opExtrude","SWEPT_FACE",FACE,{"disambiguationData":[OSD([sQuery(id+"F34.wireOp",EDGE,"E22")])]})]});
            chamfer(context, id + "F36", {"entities" : qUnion([Q0, Q1, Q2, Q3]), "width" : 1.27 * mm, "tangentPropagation" : true});
        }
        {
            var Q0;
            Q0=makeQuery(id+"F29.opExtrude","CAP_EDGE",EDGE,{"disambiguationData":[OSD([sQuery(id+"F27.wireOp",EDGE,"E17")])],"isStart":true});
            var Q1;
            {var subQ0=sQuery(id+"F25.wireOp",EDGE,"E13.top");Q1=makeQuery(id+"F30.opBoolean","MERGE",FACE,{"derivedFrom":[makeQuery(id+"F26.opExtrude","SWEPT_FACE",FACE,{"disambiguationData":[OSD([subQ0,sQuery(id+"F25.wireOp",EDGE,"E14.bottom")])]}),makeQuery(id+"F29.opExtrude","CAP_FACE",FACE,{"disambiguationData":[OSD([subQ0,sQuery(id+"F25.wireOp",EDGE,"E13.left"),sQuery(id+"F27.wireOp",EDGE,"E16"),sQuery(id+"F27.wireOp",EDGE,"E17")])],"isStart":true})]});}
            var Q2;
            Q2=makeQuery(id+"F29.opExtrude","SWEPT_EDGE",EDGE,{"disambiguationData":[OSD([sQuery(id+"F27.wireOp",EDGE,"E16"),sQuery(id+"F27.wireOp",EDGE,"E17")])]});
            var Q3;
            {var subQ0=sQuery(id+"F25.wireOp",EDGE,"E13.left");Q3=makeQuery(id+"F30.opBoolean","MERGE",EDGE,{"derivedFrom":[makeQuery(id+"F26.opExtrude","CAP_EDGE",EDGE,{"disambiguationData":[OSD([subQ0])],"isStart":false}),makeQuery(id+"F29.opExtrude","SWEPT_EDGE",EDGE,{"disambiguationData":[OSD([sQuery(id+"F25.wireOp",EDGE,"E13.top"),subQ0,sQuery(id+"F25.wireOp",EDGE,"E14.bottom"),sQuery(id+"F27.wireOp",EDGE,"E17")])]})]});}
            var Q4;
            {var subQ0=sQuery(id+"F25.wireOp",EDGE,"E13.left");Q4=makeQuery(id+"F30.opBoolean","MERGE",EDGE,{"derivedFrom":[makeQuery(id+"F26.opExtrude","CAP_EDGE",EDGE,{"disambiguationData":[OSD([subQ0])],"isStart":true}),makeQuery(id+"F29.opExtrude","SWEPT_EDGE",EDGE,{"disambiguationData":[OSD([sQuery(id+"F25.wireOp",EDGE,"E13.top"),subQ0,sQuery(id+"F25.wireOp",EDGE,"E14.bottom"),sQuery(id+"F27.wireOp",EDGE,"E16")])]})]});}
            var Q5;
            Q5=makeQuery(id+"F30.opBoolean","MERGE",FACE,{"derivedFrom":[makeQuery(id+"F26.opExtrude","SWEPT_FACE",FACE,{"disambiguationData":[OSD([sQuery(id+"F25.wireOp",EDGE,"E13.bottom"),sQuery(id+"F25.wireOp",EDGE,"E15.bottom")])]}),makeQuery(id+"F29.opExtrude","CAP_FACE",FACE,{"disambiguationData":[OSD([sQuery(id+"F25.wireOp",EDGE,"E13.top"),sQuery(id+"F25.wireOp",EDGE,"E13.left"),sQuery(id+"F27.wireOp",EDGE,"E16"),sQuery(id+"F27.wireOp",EDGE,"E17")])],"isStart":false})]});
            fillet(context, id + "F37", {"entities" : qUnion([Q0, Q1, Q2, Q3, Q4, Q5]), "radius" : 1.9 * mm, "tangentPropagation" : true, "allowEdgeOverflow" : false});
        }
        {
            var Q0;
            Q0=makeQuery(id+"F26.opExtrude","SWEPT_FACE",FACE,{"disambiguationData":[OSD([sQuery(id+"F25.wireOp",EDGE,"E15.top")])]});
            var sketch = newSketch(context, id + "F38", { "sketchPlane" : qUnion([Q0])});
            skCircle(sketch, "E23", {"center": v(-1.2, 12.7) * mm, "radius": 1.59 * mm});
            skSolve(sketch);
        }
        {
            var Q0;
            Q0=makeQuery(id+"F38.imprint","IMPRINT",FACE,{"disambiguationData":[TD([[makeQuery(id+"F38.imprint","IMPRINT",EDGE,{"derivedFrom":sQuery(id+"F38.wireOp",EDGE,"E23")}),1.0]])]});
            extrude(context, id + "F39", {"entities" : qUnion([Q0]), "operationType" : NewBodyOperationType.REMOVE, "endBound" : BoundingType.SYMMETRIC, "depth" : 127 * mm});
        }
    });
